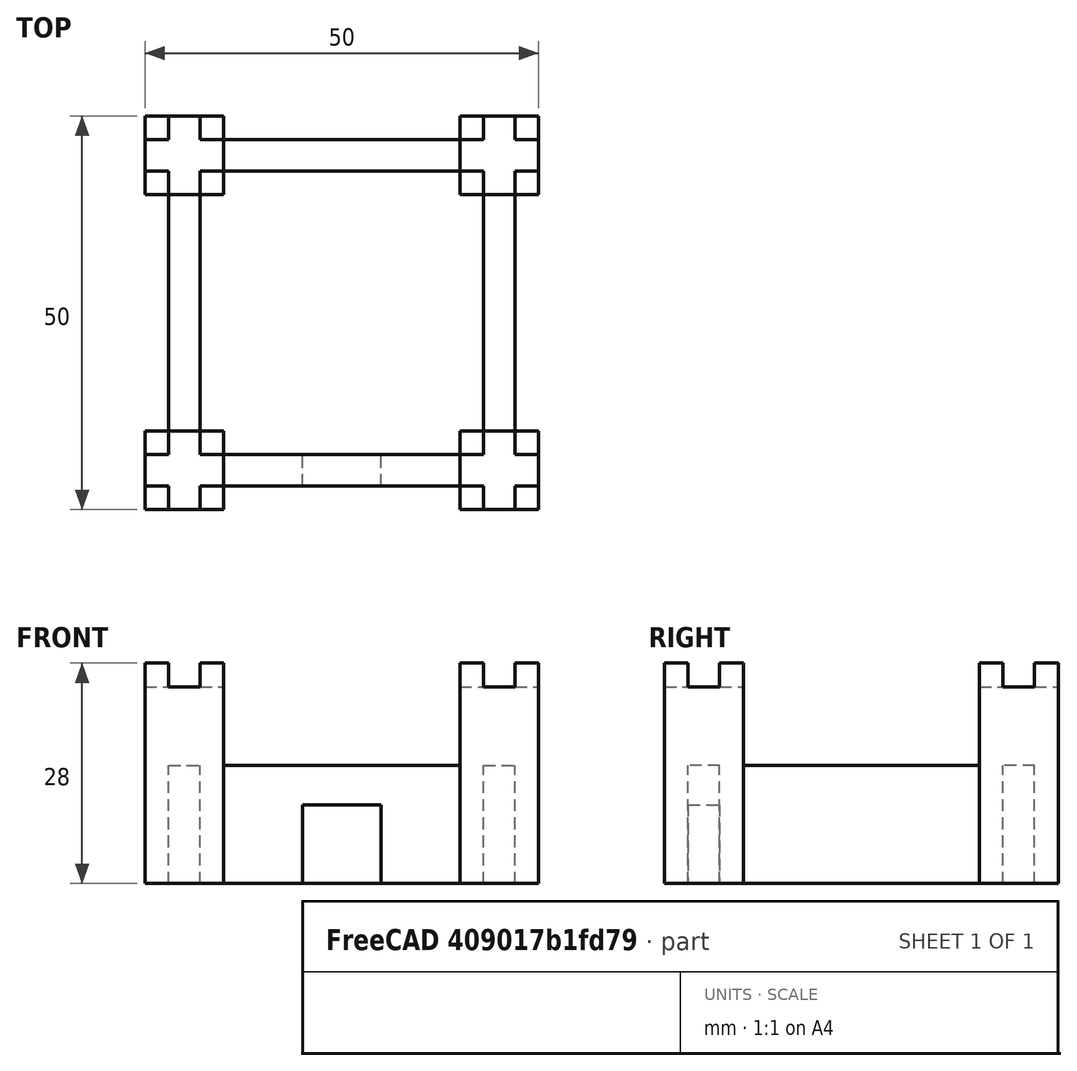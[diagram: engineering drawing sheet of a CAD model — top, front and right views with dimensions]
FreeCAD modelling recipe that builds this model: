
FCSTD DOCUMENT  (FreeCAD 0.20R29177 +233 (Git))
Label: Reto_5_castillo
License: Creative Commons Attribution-ShareAlike
LicenseURL: http://creativecommons.org/licenses/by-sa/4.0/
objects: Part::Box×25, Part::MultiFuse×5, Part::Cut×1
note: 31 computed .brp shape members not serialized (recipe doc carries the construction recipe); baked Part::Feature solids carry a one-line shape summary decoded from their .brp

FEATURE [Part::Box] Box  label="wall"
  AttacherType = Attacher::AttachEngine3D
  Height = 15
  Length = 50
  Placement = pos=(0,3,0) rot=(0,0,1;0rad)
  Width = 4
FEATURE [Part::Box] Box001  label="Cubo"
  AttacherType = Attacher::AttachEngine3D
  Height = 25
  Length = 10
  Width = 10
FEATURE [Part::Box] Box002  label="Cubo001"
  AttacherType = Attacher::AttachEngine3D
  Height = 3
  Length = 3
  Placement = pos=(0,0,25) rot=(0,0,1;0rad)
  Width = 3
FEATURE [Part::Box] Box003  label="Cubo002"
  AttacherType = Attacher::AttachEngine3D
  Height = 3
  Length = 3
  Placement = pos=(7,0,25) rot=(0,0,1;0rad)
  Width = 3
FEATURE [Part::Box] Box004  label="Cubo003"
  AttacherType = Attacher::AttachEngine3D
  Height = 3
  Length = 3
  Placement = pos=(7,7,25) rot=(0,0,1;0rad)
  Width = 3
FEATURE [Part::Box] Box005  label="Cubo004"
  AttacherType = Attacher::AttachEngine3D
  Height = 3
  Length = 3
  Placement = pos=(0,7,25) rot=(0,0,1;0rad)
  Width = 3
FEATURE [Part::MultiFuse] Fusion
  Shapes = -> [Box001,Box002,Box003,Box004,Box005]
FEATURE [Part::Box] Box006  label="Cubo005"
  AttacherType = Attacher::AttachEngine3D
  Height = 25
  Length = 10
  Width = 10
FEATURE [Part::Box] Box007  label="Cubo006"
  AttacherType = Attacher::AttachEngine3D
  Height = 3
  Length = 3
  Placement = pos=(0,0,25) rot=(0,0,1;0rad)
  Width = 3
FEATURE [Part::Box] Box008  label="Cubo007"
  AttacherType = Attacher::AttachEngine3D
  Height = 3
  Length = 3
  Placement = pos=(7,0,25) rot=(0,0,1;0rad)
  Width = 3
FEATURE [Part::Box] Box009  label="Cubo008"
  AttacherType = Attacher::AttachEngine3D
  Height = 3
  Length = 3
  Placement = pos=(7,7,25) rot=(0,0,1;0rad)
  Width = 3
FEATURE [Part::Box] Box010  label="Cubo009"
  AttacherType = Attacher::AttachEngine3D
  Height = 3
  Length = 3
  Placement = pos=(0,7,25) rot=(0,0,1;0rad)
  Width = 3
FEATURE [Part::MultiFuse] Fusion001
  Placement = pos=(40,0,0) rot=(0,0,1;0rad)
  Shapes = -> [Box006,Box007,Box008,Box009,Box010]
FEATURE [Part::Box] Box011  label="Cubo010"
  AttacherType = Attacher::AttachEngine3D
  Height = 25
  Length = 10
  Width = 10
FEATURE [Part::Box] Box012  label="Cubo011"
  AttacherType = Attacher::AttachEngine3D
  Height = 3
  Length = 3
  Placement = pos=(0,0,25) rot=(0,0,1;0rad)
  Width = 3
FEATURE [Part::Box] Box013  label="Cubo012"
  AttacherType = Attacher::AttachEngine3D
  Height = 3
  Length = 3
  Placement = pos=(7,0,25) rot=(0,0,1;0rad)
  Width = 3
FEATURE [Part::Box] Box014  label="Cubo013"
  AttacherType = Attacher::AttachEngine3D
  Height = 3
  Length = 3
  Placement = pos=(7,7,25) rot=(0,0,1;0rad)
  Width = 3
FEATURE [Part::Box] Box015  label="Cubo014"
  AttacherType = Attacher::AttachEngine3D
  Height = 3
  Length = 3
  Placement = pos=(0,7,25) rot=(0,0,1;0rad)
  Width = 3
FEATURE [Part::MultiFuse] Fusion002
  Placement = pos=(40,40,0) rot=(0,0,1;0rad)
  Shapes = -> [Box011,Box012,Box013,Box014,Box015]
FEATURE [Part::Box] Box016  label="Cubo015"
  AttacherType = Attacher::AttachEngine3D
  Height = 25
  Length = 10
  Width = 10
FEATURE [Part::Box] Box017  label="Cubo016"
  AttacherType = Attacher::AttachEngine3D
  Height = 3
  Length = 3
  Placement = pos=(0,0,25) rot=(0,0,1;0rad)
  Width = 3
FEATURE [Part::Box] Box018  label="Cubo017"
  AttacherType = Attacher::AttachEngine3D
  Height = 3
  Length = 3
  Placement = pos=(7,0,25) rot=(0,0,1;0rad)
  Width = 3
FEATURE [Part::Box] Box019  label="Cubo018"
  AttacherType = Attacher::AttachEngine3D
  Height = 3
  Length = 3
  Placement = pos=(7,7,25) rot=(0,0,1;0rad)
  Width = 3
FEATURE [Part::Box] Box020  label="Cubo019"
  AttacherType = Attacher::AttachEngine3D
  Height = 3
  Length = 3
  Placement = pos=(0,7,25) rot=(0,0,1;0rad)
  Width = 3
FEATURE [Part::MultiFuse] Fusion003
  Placement = pos=(0,40,0) rot=(0,0,1;0rad)
  Shapes = -> [Box016,Box017,Box018,Box019,Box020]
FEATURE [Part::Box] Box021  label="wall001"
  AttacherType = Attacher::AttachEngine3D
  Height = 15
  Length = 50
  Placement = pos=(0,43,0) rot=(0,0,1;0rad)
  Width = 4
FEATURE [Part::Box] Box022  label="wall002"
  AttacherType = Attacher::AttachEngine3D
  Height = 15
  Length = 50
  Placement = pos=(7,0,0) rot=(0,0,1;1.5708rad)
  Width = 4
FEATURE [Part::Box] Box023  label="wall003"
  AttacherType = Attacher::AttachEngine3D
  Height = 15
  Length = 50
  Placement = pos=(47,0,0) rot=(0,0,1;1.5708rad)
  Width = 4
FEATURE [Part::Box] Box024  label="Cubo020"
  AttacherType = Attacher::AttachEngine3D
  Height = 10
  Length = 10
  Placement = pos=(20,0,0) rot=(0,0,1;0rad)
  Width = 10
FEATURE [Part::Cut] Cut
  Base = -> Box
  Tool = -> Box024
FEATURE [Part::MultiFuse] Fusion004
  Shapes = -> [Fusion001,Fusion,Fusion002,Fusion003,Box021,Box022,Box023,Cut]
